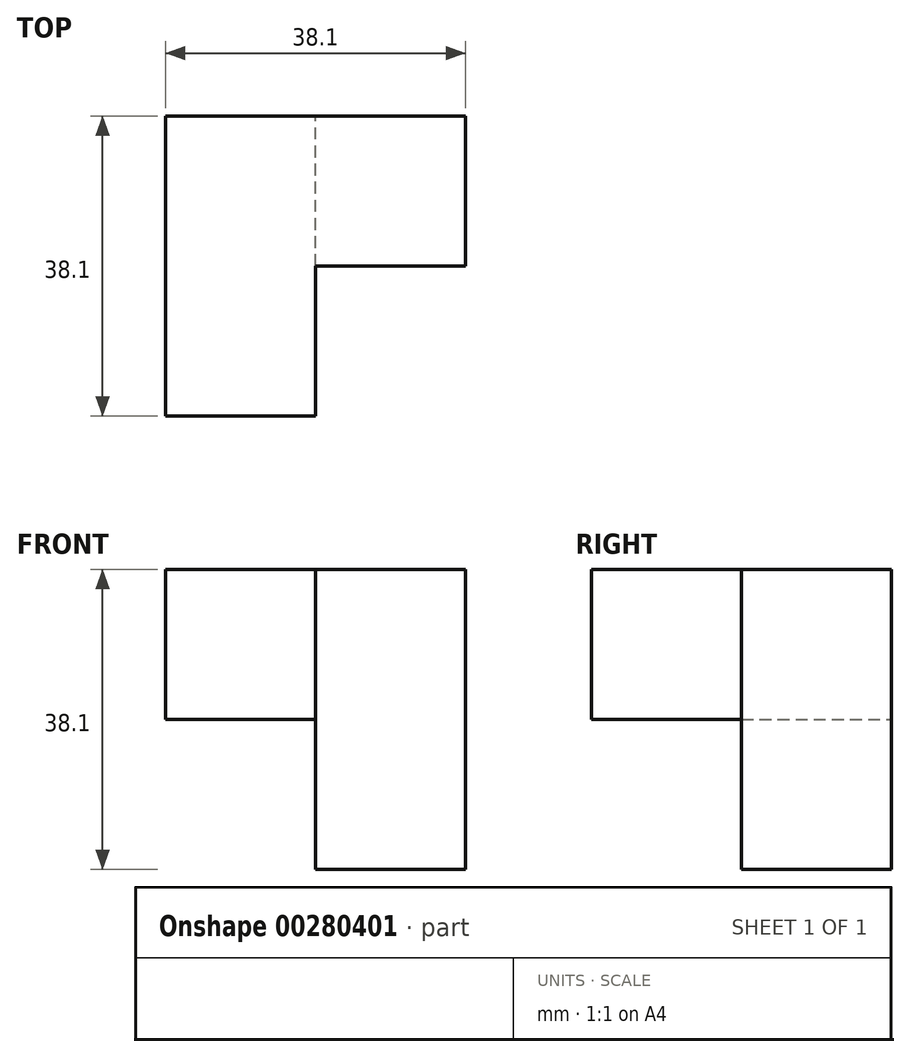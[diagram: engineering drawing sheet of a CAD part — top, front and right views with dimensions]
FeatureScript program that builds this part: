
annotation { "Feature Type Name" : "Feature", "Feature Type Description" : "" }
export const myFeature = defineFeature(function(context is Context, id is Id, definition is map)
    precondition{}
    {
        {
            var Q0;
            Q0=qCreatedBy(makeId("Top.planeOp"),FACE);
            var sketch = newSketch(context, id + "F0", { "sketchPlane" : qUnion([Q0])});
            skLineSegment(sketch, "E0.bottom", {"start": v(0, 0) * mm, "end": v(19.05, 0) * mm});
            skLineSegment(sketch, "E0.top", {"start": v(0, 38.1) * mm, "end": v(38.1, 38.1) * mm});
            skLineSegment(sketch, "E0.left", {"start": v(0, 0) * mm, "end": v(0, 38.1) * mm});
            skLineSegment(sketch, "E0.right", {"start": v(38.1, 19.05) * mm, "end": v(38.1, 38.1) * mm});
            skLineSegment(sketch, "E1", {"start": v(38.1, 19.05) * mm, "end": v(19.05, 19.05) * mm});
            skLineSegment(sketch, "E2", {"start": v(19.05, 19.05) * mm, "end": v(19.05, 0) * mm});
            skPoint(sketch, "E3.orphan", {"position": v(38.1, 0) * mm});
            skSolve(sketch);
        }
        {
            var Q0;
            Q0 = qSketchRegion(id + "F0", true);
            extrude(context, id + "F1", {"entities" : qUnion([Q0]), "depth" : 19.05 * mm});
        }
        {
            var Q0;
            Q0=makeQuery(id+"F1.opExtrude","CAP_FACE",FACE,{"disambiguationData":[OSD([sQuery(id+"F0.wireOp",EDGE,"E0.bottom"),sQuery(id+"F0.wireOp",EDGE,"E0.top"),sQuery(id+"F0.wireOp",EDGE,"E0.left"),sQuery(id+"F0.wireOp",EDGE,"E0.right"),sQuery(id+"F0.wireOp",EDGE,"E1"),sQuery(id+"F0.wireOp",EDGE,"E2")])],"isStart":true});
            var sketch = newSketch(context, id + "F2", { "sketchPlane" : qUnion([Q0])});
            skLineSegment(sketch, "E4.bottom", {"start": v(19.05, -19.05) * mm, "end": v(38.1, -19.05) * mm});
            skLineSegment(sketch, "E4.top", {"start": v(19.05, -38.1) * mm, "end": v(38.1, -38.1) * mm});
            skLineSegment(sketch, "E4.left", {"start": v(19.05, -19.05) * mm, "end": v(19.05, -38.1) * mm});
            skLineSegment(sketch, "E4.right", {"start": v(38.1, -19.05) * mm, "end": v(38.1, -38.1) * mm});
            skSolve(sketch);
        }
        {
            var Q0;
            Q0 = qSketchRegion(id + "F2", true);
            extrude(context, id + "F3", {"entities" : qUnion([Q0]), "operationType" : NewBodyOperationType.ADD, "depth" : 19.05 * mm});
        }
    });
